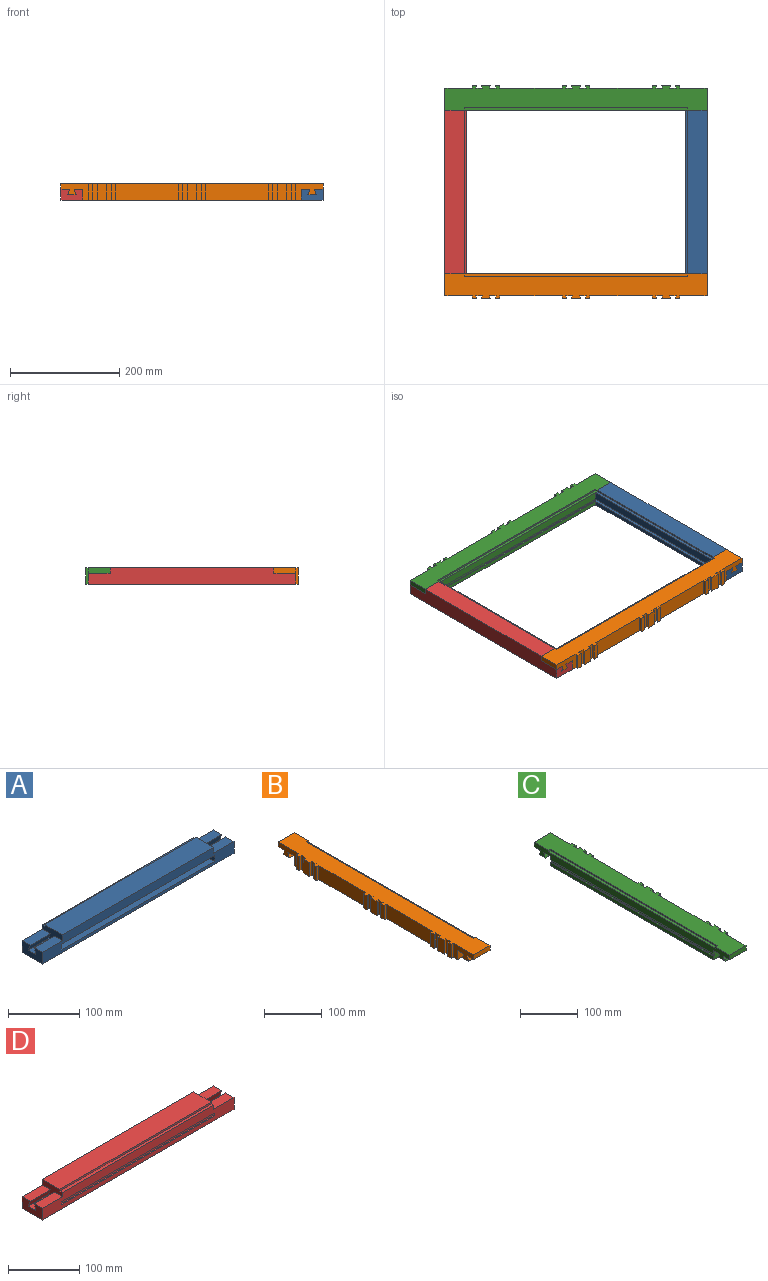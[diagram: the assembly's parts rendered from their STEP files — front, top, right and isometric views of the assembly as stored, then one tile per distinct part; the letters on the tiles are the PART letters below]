
ASSEMBLY  parts=4 mates=3
PART A: 28 faces, bbox 380x40x30 mm
  f0: plane 304x2.5mm, normal (0,-1,0), area 760mm2, adj f22,f23,f24,f26
  f1: plane 40x17.5mm, normal (1,0,0), area 465.5mm2, adj f3,f5,f6,f7,f8,f17,f18,f19
  f2: plane 40x17.5mm, normal (-1,0,0), area 465.5mm2, adj f6,f7,f8,f12,f13,f15,f16,f19
  f3: plane 40x10mm, normal (0,0.94,-0.34), area 420.4mm2, adj f1,f4,f10,f18,f22,f26
  f4: plane 38x15.28mm, normal (0,0,1), area 580.6mm2, adj f3,f5,f10,f22
  f5: plane 40x10mm, normal (0,-0.94,-0.34), area 420.4mm2, adj f1,f4,f10,f17,f22,f26
  f6: plane 300x35mm, normal (0,0,1), area 10500mm2, adj f1,f2,f7,f20
  f7: plane 380x30mm, normal (0,-1,0), area 7560mm2, adj f1,f2,f6,f9,f10,f11,f16,f18
  f8: plane 380x27mm, normal (0,1,0), area 8180mm2, adj f1,f2,f9,f10,f11,f12,f17,f19
  f9: plane 40x20mm, normal (-1,0,0), area 683.6mm2, adj f7,f8,f11,f12,f13,f14,f15,f16
  f10: plane 40x20mm, normal (1,0,0), area 683.6mm2, adj f3,f4,f5,f7,f8,f11,f17,f18
  f11: plane 380x40mm, normal (0,0,-1), area 15200mm2, adj f7,f8,f9,f10
  f12: plane 40x16mm, normal (0,0,1), area 640mm2, adj f2,f8,f9,f13
  f13: plane 40x10mm, normal (0,-0.94,-0.34), area 420.4mm2, adj f2,f9,f12,f14,f24,f26
  f14: plane 38x15.28mm, normal (0,0,1), area 580.6mm2, adj f9,f13,f15,f24
  f15: plane 40x10mm, normal (0,0.94,-0.34), area 420.4mm2, adj f2,f9,f14,f16,f24,f26
  f16: plane 40x16mm, normal (0,0,1), area 640mm2, adj f2,f7,f9,f15
  f17: plane 40x16mm, normal (0,0,1), area 640mm2, adj f1,f5,f8,f10
  f18: plane 40x16mm, normal (0,0,1), area 640mm2, adj f1,f3,f7,f10
  f19: plane 300x5mm, normal (0,0,1), area 1500mm2, adj f1,f2,f8,f20
  f20: plane 300x3mm, normal (0,1,0), area 900mm2, adj f1,f2,f6,f19
  f21: plane 304x10mm, normal (0,0,1), area 3040mm2, adj f7,f22,f24,f25
  f22: plane 40x10mm, normal (-1,0,0), area 214.1mm2, adj f0,f3,f4,f5,f7,f8,f21,f23
  f23: plane 304x10mm, normal (0,0,-1), area 3040mm2, adj f0,f7,f22,f24
  f24: plane 40x10mm, normal (1,0,0), area 214.1mm2, adj f0,f7,f8,f13,f14,f15,f21,f23
  f25: plane 304x2.5mm, normal (0,-1,0), area 760mm2, adj f21,f22,f24,f27
  f26: plane 304x30mm, normal (0,0,-1), area 9066.2mm2, adj f0,f1,f2,f3,f5,f8,f13,f15
  f27: plane 304x30mm, normal (0,0,1), area 9120mm2, adj f8,f22,f24,f25
PART B: 64 faces, bbox 45x480x30 mm
  f0: plane 480x20mm, normal (1,0,0), area 6766.9mm2, adj f1,f2,f4,f25,f26,f45,f46,f47
  f1: plane 40x20mm, normal (0,1,0), area 790mm2, adj f0,f3,f5,f6,f49,f61,f62,f63
  f2: plane 40x20mm, normal (0,-1,0), area 790mm2, adj f0,f3,f5,f24,f50,f61,f62,f63
  f3: plane 400x7.5mm, normal (1,0,0), area 3000mm2, adj f1,f2,f5,f61
  f4: plane 480x45mm, normal (0,0,1), area 17595.4mm2, adj f0,f6,f7,f8,f9,f10,f11,f12
  f5: plane 400x45mm, normal (0,0,-1), area 16445.4mm2, adj f1,f2,f3,f6,f7,f8,f9,f10
  f6: plane 50x30mm, normal (-1,0,0), area 816.4mm2, adj f1,f4,f5,f26,f27,f45,f46,f47
  f7: plane 30x5mm, normal (0.34,-0.94,0), area 159.6mm2, adj f4,f5,f8,f44
  f8: plane 30x11.97mm, normal (-1,0,0), area 359.2mm2, adj f4,f5,f7,f9
  f9: plane 30x5mm, normal (0.34,0.94,0), area 159.6mm2, adj f4,f5,f8,f10
  f10: plane 30x8.33mm, normal (-1,0,0), area 250mm2, adj f4,f5,f9,f11
  f11: plane 30x5mm, normal (0,-1,0), area 150mm2, adj f4,f5,f10,f12
  f12: plane 115x30mm, normal (-1,0,0), area 3450mm2, adj f4,f5,f11,f13
  f13: plane 30x5mm, normal (0,1,0), area 150mm2, adj f4,f5,f12,f14
  f14: plane 30x8.33mm, normal (-1,0,0), area 250mm2, adj f4,f5,f13,f15
  f15: plane 30x5mm, normal (0.34,-0.94,0), area 159.6mm2, adj f4,f5,f14,f16
  f16: plane 30x11.97mm, normal (-1,0,0), area 359.2mm2, adj f4,f5,f15,f17
  f17: plane 30x5mm, normal (0.34,0.94,0), area 159.6mm2, adj f4,f5,f16,f18
  f18: plane 30x16.67mm, normal (-1,0,0), area 500mm2, adj f4,f5,f17,f19
  f19: plane 30x5mm, normal (0.34,-0.94,0), area 159.6mm2, adj f4,f5,f18,f20
  f20: plane 30x11.97mm, normal (-1,0,0), area 359.2mm2, adj f4,f5,f19,f21
  f21: plane 30x5mm, normal (0.34,0.94,0), area 159.6mm2, adj f4,f5,f20,f22
  f22: plane 30x8.33mm, normal (-1,0,0), area 250mm2, adj f4,f5,f21,f23
  f23: plane 30x5mm, normal (0,-1,0), area 150mm2, adj f4,f5,f22,f24
  f24: plane 50x30mm, normal (-1,0,0), area 816.4mm2, adj f2,f4,f5,f23,f25,f50,f51,f52
  f25: plane 40x10mm, normal (0,-1,0), area 400mm2, adj f0,f4,f24,f52
  f26: plane 40x10mm, normal (0,1,0), area 400mm2, adj f0,f4,f6,f45
  f27: plane 30x5mm, normal (0,1,0), area 150mm2, adj f4,f5,f6,f28
  f28: plane 30x8.33mm, normal (-1,0,0), area 250mm2, adj f4,f5,f27,f29
  f29: plane 30x5mm, normal (0.34,-0.94,0), area 159.6mm2, adj f4,f5,f28,f30
  f30: plane 30x11.97mm, normal (-1,0,0), area 359.2mm2, adj f4,f5,f29,f31
  f31: plane 30x5mm, normal (0.34,0.94,0), area 159.6mm2, adj f4,f5,f30,f32
  f32: plane 30x16.67mm, normal (-1,0,0), area 500mm2, adj f4,f5,f31,f33
  f33: plane 30x5mm, normal (0.34,-0.94,0), area 159.6mm2, adj f4,f5,f32,f34
  f34: plane 30x11.97mm, normal (-1,0,0), area 359.2mm2, adj f4,f5,f33,f35
  f35: plane 30x5mm, normal (0.34,0.94,0), area 159.6mm2, adj f4,f5,f34,f36
  f36: plane 30x8.33mm, normal (-1,0,0), area 250mm2, adj f4,f5,f35,f37
  f37: plane 30x5mm, normal (0,-1,0), area 150mm2, adj f4,f5,f36,f38
  f38: plane 115x30mm, normal (-1,0,0), area 3450mm2, adj f4,f5,f37,f39
  f39: plane 30x5mm, normal (0,1,0), area 150mm2, adj f4,f5,f38,f40
  f40: plane 30x8.33mm, normal (-1,0,0), area 250mm2, adj f4,f5,f39,f41
  f41: plane 30x5mm, normal (0.34,-0.94,0), area 159.6mm2, adj f4,f5,f40,f42
  f42: plane 30x11.97mm, normal (-1,0,0), area 359.2mm2, adj f4,f5,f41,f43
  f43: plane 30x5mm, normal (0.34,0.94,0), area 159.6mm2, adj f4,f5,f42,f44
  f44: plane 30x16.67mm, normal (-1,0,0), area 500mm2, adj f4,f5,f7,f43
  f45: plane 40x16mm, normal (0,0,-1), area 640mm2, adj f0,f6,f26,f47
  f46: plane 40x15.28mm, normal (0,0,-1), area 611.2mm2, adj f0,f6,f47,f48
  f47: plane 40x10mm, normal (0,0.94,0.34), area 425.7mm2, adj f0,f6,f45,f46
  f48: plane 40x10mm, normal (0,-0.94,0.34), area 425.7mm2, adj f0,f6,f46,f49
  f49: plane 40x16mm, normal (0,0,-1), area 640mm2, adj f0,f1,f6,f48
  f50: plane 40x16mm, normal (0,0,-1), area 640mm2, adj f0,f2,f24,f51
  f51: plane 40x10mm, normal (0,0.94,0.34), area 420.4mm2, adj f0,f24,f50,f53,f59,f60
  f52: plane 40x16mm, normal (0,0,-1), area 640mm2, adj f0,f24,f25,f54
  f53: plane 38x15.28mm, normal (0,0,-1), area 580.6mm2, adj f24,f51,f54,f60
  f54: plane 40x10mm, normal (0,-0.94,0.34), area 420.4mm2, adj f0,f24,f52,f53,f59,f60
  f55: plane 5x3mm, normal (0,-1,0), area 15mm2, adj f0,f4,f57,f58
  f56: plane 5x3mm, normal (0,1,0), area 15mm2, adj f0,f4,f57,f58
  f57: plane 410x5mm, normal (0,0,1), area 2050mm2, adj f0,f55,f56,f58
  f58: plane 410x3mm, normal (1,0,0), area 1230mm2, adj f4,f55,f56,f57
  f59: plane 13.46x2mm, normal (0,0,-1), area 26.9mm2, adj f0,f51,f54,f60
  f60: plane 15.28x2.5mm, normal (1,0,0), area 35.9mm2, adj f51,f53,f54,f59
  f61: plane 400x2mm, normal (0,0,1), area 800mm2, adj f1,f2,f3,f62
  f62: plane 400x5mm, normal (1,0,0), area 2000mm2, adj f1,f2,f61,f63
  f63: plane 400x2mm, normal (0,0,-1), area 800mm2, adj f0,f1,f2,f62
PART C: 64 faces, bbox 45x480x30 mm
  f0: plane 480x20mm, normal (-1,0,0), area 6766.9mm2, adj f2,f3,f4,f5,f7,f28,f29,f48
  f1: plane 38x15.28mm, normal (0,0,-1), area 580.6mm2, adj f2,f3,f9,f63
  f2: plane 40x10mm, normal (0,-0.94,0.34), area 420.4mm2, adj f0,f1,f9,f48,f62,f63
  f3: plane 40x10mm, normal (0,0.94,0.34), area 420.4mm2, adj f0,f1,f9,f49,f62,f63
  f4: plane 40x20mm, normal (0,-1,0), area 790mm2, adj f0,f6,f8,f9,f49,f59,f60,f61
  f5: plane 40x20mm, normal (0,1,0), area 790mm2, adj f0,f6,f8,f27,f50,f59,f60,f61
  f6: plane 400x7.5mm, normal (-1,0,0), area 3000mm2, adj f4,f5,f8,f60
  f7: plane 480x45mm, normal (0,0,1), area 17595.4mm2, adj f0,f9,f10,f11,f12,f13,f14,f15
  f8: plane 400x45mm, normal (0,0,-1), area 16445.4mm2, adj f4,f5,f6,f9,f10,f11,f12,f13
  f9: plane 50x30mm, normal (1,0,0), area 816.4mm2, adj f1,f2,f3,f4,f7,f8,f29,f30
  f10: plane 30x5mm, normal (-0.34,0.94,0), area 159.6mm2, adj f7,f8,f11,f47
  f11: plane 30x11.97mm, normal (1,0,0), area 359.2mm2, adj f7,f8,f10,f12
  f12: plane 30x5mm, normal (-0.34,-0.94,0), area 159.6mm2, adj f7,f8,f11,f13
  f13: plane 30x8.33mm, normal (1,0,0), area 250mm2, adj f7,f8,f12,f14
  f14: plane 30x5mm, normal (0,1,0), area 150mm2, adj f7,f8,f13,f15
  f15: plane 115x30mm, normal (1,0,0), area 3450mm2, adj f7,f8,f14,f16
  f16: plane 30x5mm, normal (0,-1,0), area 150mm2, adj f7,f8,f15,f17
  f17: plane 30x8.33mm, normal (1,0,0), area 250mm2, adj f7,f8,f16,f18
  f18: plane 30x5mm, normal (-0.34,0.94,0), area 159.6mm2, adj f7,f8,f17,f19
  f19: plane 30x11.97mm, normal (1,0,0), area 359.2mm2, adj f7,f8,f18,f20
  f20: plane 30x5mm, normal (-0.34,-0.94,0), area 159.6mm2, adj f7,f8,f19,f21
  f21: plane 30x16.67mm, normal (1,0,0), area 500mm2, adj f7,f8,f20,f22
  f22: plane 30x5mm, normal (-0.34,0.94,0), area 159.6mm2, adj f7,f8,f21,f23
  f23: plane 30x11.97mm, normal (1,0,0), area 359.2mm2, adj f7,f8,f22,f24
  f24: plane 30x5mm, normal (-0.34,-0.94,0), area 159.6mm2, adj f7,f8,f23,f25
  f25: plane 30x8.33mm, normal (1,0,0), area 250mm2, adj f7,f8,f24,f26
  f26: plane 30x5mm, normal (0,1,0), area 150mm2, adj f7,f8,f25,f27
  f27: plane 50x30mm, normal (1,0,0), area 816.4mm2, adj f5,f7,f8,f26,f28,f50,f51,f52
  f28: plane 40x10mm, normal (0,1,0), area 400mm2, adj f0,f7,f27,f52
  f29: plane 40x10mm, normal (0,-1,0), area 400mm2, adj f0,f7,f9,f48
  f30: plane 30x5mm, normal (0,-1,0), area 150mm2, adj f7,f8,f9,f31
  f31: plane 30x8.33mm, normal (1,0,0), area 250mm2, adj f7,f8,f30,f32
  f32: plane 30x5mm, normal (-0.34,0.94,0), area 159.6mm2, adj f7,f8,f31,f33
  f33: plane 30x11.97mm, normal (1,0,0), area 359.2mm2, adj f7,f8,f32,f34
  f34: plane 30x5mm, normal (-0.34,-0.94,0), area 159.6mm2, adj f7,f8,f33,f35
  f35: plane 30x16.67mm, normal (1,0,0), area 500mm2, adj f7,f8,f34,f36
  f36: plane 30x5mm, normal (-0.34,0.94,0), area 159.6mm2, adj f7,f8,f35,f37
  f37: plane 30x11.97mm, normal (1,0,0), area 359.2mm2, adj f7,f8,f36,f38
  f38: plane 30x5mm, normal (-0.34,-0.94,0), area 159.6mm2, adj f7,f8,f37,f39
  f39: plane 30x8.33mm, normal (1,0,0), area 250mm2, adj f7,f8,f38,f40
  f40: plane 30x5mm, normal (0,1,0), area 150mm2, adj f7,f8,f39,f41
  f41: plane 115x30mm, normal (1,0,0), area 3450mm2, adj f7,f8,f40,f42
  f42: plane 30x5mm, normal (0,-1,0), area 150mm2, adj f7,f8,f41,f43
  f43: plane 30x8.33mm, normal (1,0,0), area 250mm2, adj f7,f8,f42,f44
  f44: plane 30x5mm, normal (-0.34,0.94,0), area 159.6mm2, adj f7,f8,f43,f45
  f45: plane 30x11.97mm, normal (1,0,0), area 359.2mm2, adj f7,f8,f44,f46
  f46: plane 30x5mm, normal (-0.34,-0.94,0), area 159.6mm2, adj f7,f8,f45,f47
  f47: plane 30x16.67mm, normal (1,0,0), area 500mm2, adj f7,f8,f10,f46
  f48: plane 40x16mm, normal (0,0,-1), area 640mm2, adj f0,f2,f9,f29
  f49: plane 40x16mm, normal (0,0,-1), area 640mm2, adj f0,f3,f4,f9
  f50: plane 40x16mm, normal (0,0,-1), area 640mm2, adj f0,f5,f27,f51
  f51: plane 40x10mm, normal (0,-0.94,0.34), area 425.7mm2, adj f0,f27,f50,f53
  f52: plane 40x16mm, normal (0,0,-1), area 640mm2, adj f0,f27,f28,f54
  f53: plane 40x15.28mm, normal (0,0,-1), area 611.2mm2, adj f0,f27,f51,f54
  f54: plane 40x10mm, normal (0,0.94,0.34), area 425.7mm2, adj f0,f27,f52,f53
  f55: plane 5x3mm, normal (0,1,0), area 15mm2, adj f0,f7,f57,f58
  f56: plane 5x3mm, normal (0,-1,0), area 15mm2, adj f0,f7,f57,f58
  f57: plane 410x5mm, normal (0,0,1), area 2050mm2, adj f0,f55,f56,f58
  f58: plane 410x3mm, normal (-1,0,0), area 1230mm2, adj f7,f55,f56,f57
  f59: plane 400x5mm, normal (-1,0,0), area 2000mm2, adj f4,f5,f60,f61
  f60: plane 400x2mm, normal (0,0,1), area 800mm2, adj f4,f5,f6,f59
  f61: plane 400x2mm, normal (0,0,-1), area 800mm2, adj f0,f4,f5,f59
  f62: plane 13.46x2mm, normal (0,0,-1), area 26.9mm2, adj f0,f2,f3,f63
  f63: plane 15.28x2.5mm, normal (-1,0,0), area 35.9mm2, adj f1,f2,f3,f62
PART D: 25 faces, bbox 380x40x30 mm
  f0: plane 300x35mm, normal (0,0,1), area 10500mm2, adj f1,f2,f12,f19
  f1: plane 40x20mm, normal (-1,0,0), area 501.4mm2, adj f0,f2,f3,f13,f14,f15,f16,f17
  f2: plane 380x30mm, normal (0,1,0), area 10600mm2, adj f0,f1,f4,f5,f6,f11,f12,f14
  f3: plane 380x27mm, normal (0,-1,0), area 8180mm2, adj f1,f4,f5,f6,f7,f12,f13,f18
  f4: plane 40x20mm, normal (1,0,0), area 683.6mm2, adj f2,f3,f6,f7,f8,f9,f10,f11
  f5: plane 40x20mm, normal (-1,0,0), area 683.6mm2, adj f2,f3,f6,f13,f14,f15,f16,f17
  f6: plane 380x40mm, normal (0,0,-1), area 15200mm2, adj f2,f3,f4,f5
  f7: plane 40x16mm, normal (0,0,1), area 640mm2, adj f3,f4,f8,f12
  f8: plane 40x10mm, normal (0,0.94,-0.34), area 425.7mm2, adj f4,f7,f9,f12
  f9: plane 40x15.28mm, normal (0,0,1), area 611.2mm2, adj f4,f8,f10,f12
  f10: plane 40x10mm, normal (0,-0.94,-0.34), area 425.7mm2, adj f4,f9,f11,f12
  f11: plane 40x16mm, normal (0,0,1), area 640mm2, adj f2,f4,f10,f12
  f12: plane 40x20mm, normal (1,0,0), area 501.4mm2, adj f0,f2,f3,f7,f8,f9,f10,f11
  f13: plane 40x16mm, normal (0,0,1), area 640mm2, adj f1,f3,f5,f17
  f14: plane 40x16mm, normal (0,0,1), area 640mm2, adj f1,f2,f5,f15
  f15: plane 40x10mm, normal (0,-0.94,-0.34), area 425.7mm2, adj f1,f5,f14,f16
  f16: plane 40x15.28mm, normal (0,0,1), area 611.2mm2, adj f1,f5,f15,f17
  f17: plane 40x10mm, normal (0,0.94,-0.34), area 425.7mm2, adj f1,f5,f13,f16
  f18: plane 300x5mm, normal (0,0,1), area 1500mm2, adj f1,f3,f12,f19
  f19: plane 300x3mm, normal (0,-1,0), area 900mm2, adj f0,f1,f12,f18
  f20: plane 304x5mm, normal (0,-1,0), area 1520mm2, adj f21,f22,f23,f24
  f21: plane 5x2mm, normal (1,0,0), area 10mm2, adj f3,f20,f22,f23
  f22: plane 304x2mm, normal (0,0,-1), area 608mm2, adj f3,f20,f21,f24
  f23: plane 304x2mm, normal (0,0,1), area 608mm2, adj f3,f20,f21,f24
  f24: plane 5x2mm, normal (-1,0,0), area 10mm2, adj f3,f20,f22,f23
PLACE A rot(axis=(0,0,1),90deg) t=(1045.31,335.72,64.74)mm
PLACE B rot(axis=(0,0,1),90deg) t=(1045.31,335.72,64.74)mm
PLACE C rot(axis=(0,0,1),90deg) t=(1045.31,335.72,64.74)mm
PLACE D rot(axis=(0,0,1),90deg) t=(1045.31,335.72,64.74)mm
MATE fastened A.f18 <-> C.f48  axis (0,0,1) through (937.31,695.72,84.74)mm
MATE fastened C.f52 <-> D.f11  axis (0,0,-1) through (473.31,695.72,84.74)mm
MATE fastened A.f16 <-> B.f52  axis (0,0,1) through (937.31,355.72,84.74)mm
